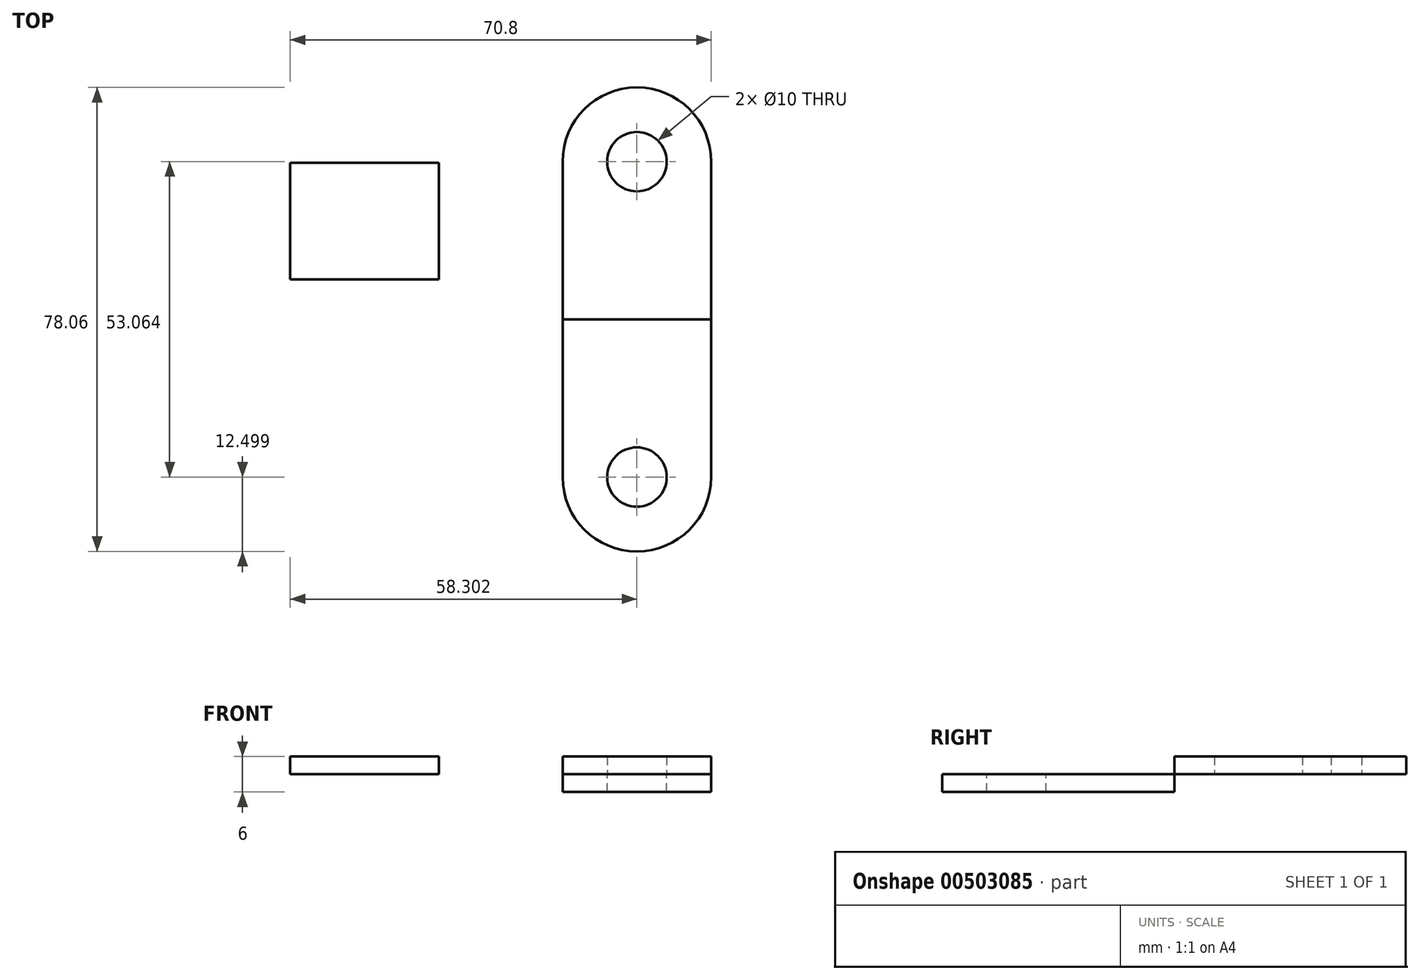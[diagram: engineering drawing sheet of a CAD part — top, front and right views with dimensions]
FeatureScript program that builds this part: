
annotation { "Feature Type Name" : "Feature", "Feature Type Description" : "" }
export const myFeature = defineFeature(function(context is Context, id is Id, definition is map)
    precondition{}
    {
        {
            var Q0;
            Q0=qCreatedBy(makeId("Top.planeOp"),FACE);
            var sketch = newSketch(context, id + "F0", { "sketchPlane" : qUnion([Q0])});
            skCircle(sketch, "E0", {"center": v(0.04, 26.48) * mm, "radius": 12.5 * mm});
            skCircle(sketch, "E1", {"center": v(0.04, -26.58) * mm, "radius": 12.5 * mm});
            skLineSegment(sketch, "E2", {"start": v(12.54, 26.48) * mm, "end": v(12.54, -26.58) * mm});
            skLineSegment(sketch, "E3", {"start": v(-12.46, 26.48) * mm, "end": v(-12.46, -26.58) * mm});
            skCircle(sketch, "E4", {"center": v(0.04, 26.48) * mm, "radius": 5 * mm});
            skCircle(sketch, "E5", {"center": v(0.04, -26.58) * mm, "radius": 5 * mm});
            skLineSegment(sketch, "E6", {"start": v(12.54, -0.05) * mm, "end": v(-12.46, -0.05) * mm});
            skLineSegment(sketch, "E7.bottom", {"start": v(-58.26, 26.32) * mm, "end": v(-33.26, 26.32) * mm});
            skLineSegment(sketch, "E7.top", {"start": v(-58.26, 6.7) * mm, "end": v(-33.26, 6.7) * mm});
            skLineSegment(sketch, "E7.left", {"start": v(-58.26, 26.32) * mm, "end": v(-58.26, 6.7) * mm});
            skLineSegment(sketch, "E7.right", {"start": v(-33.26, 26.32) * mm, "end": v(-33.26, 6.7) * mm});
            skSolve(sketch);
        }
        {
            var Q0;
            {var subQ5=sQuery(id+"F0.wireOp",EDGE,"E6");Q0=makeQuery(id+"F0.imprint","IMPRINT",FACE,{"disambiguationData":[TD([[makeQuery(id+"F0.imprint","IMPRINT",EDGE,{"derivedFrom":subQ5}),-1.0]])]});}
            var Q1;
            Q1=makeQuery(id+"F0.imprint","IMPRINT",FACE,{"disambiguationData":[TD([[makeQuery(id+"F0.imprint","IMPRINT",EDGE,{"derivedFrom":sQuery(id+"F0.wireOp",EDGE,"E4")}),-1.0]])]});
            extrude(context, id + "F1", {"entities" : qUnion([Q0, Q1]), "depth" : 3 * mm});
        }
        {
            var Q0;
            {var subQ5=sQuery(id+"F0.wireOp",EDGE,"E6");Q0=makeQuery(id+"F0.imprint","IMPRINT",FACE,{"disambiguationData":[TD([[makeQuery(id+"F0.imprint","IMPRINT",EDGE,{"derivedFrom":subQ5}),1.0]])]});}
            var Q1;
            Q1=makeQuery(id+"F0.imprint","IMPRINT",FACE,{"disambiguationData":[TD([[makeQuery(id+"F0.imprint","IMPRINT",EDGE,{"derivedFrom":sQuery(id+"F0.wireOp",EDGE,"E5")}),-1.0]])]});
            extrude(context, id + "F2", {"entities" : qUnion([Q0, Q1]), "operationType" : NewBodyOperationType.ADD, "depth" : -3 * mm});
        }
        {
            var Q0;
            Q0=makeQuery(id+"F0.imprint","IMPRINT",FACE,{"disambiguationData":[TD([[makeQuery(id+"F0.imprint","IMPRINT",EDGE,{"derivedFrom":sQuery(id+"F0.wireOp",EDGE,"E7.bottom")}),-1.0]])]});
            extrude(context, id + "F3", {"entities" : qUnion([Q0]), "depth" : 3 * mm});
        }
    });
